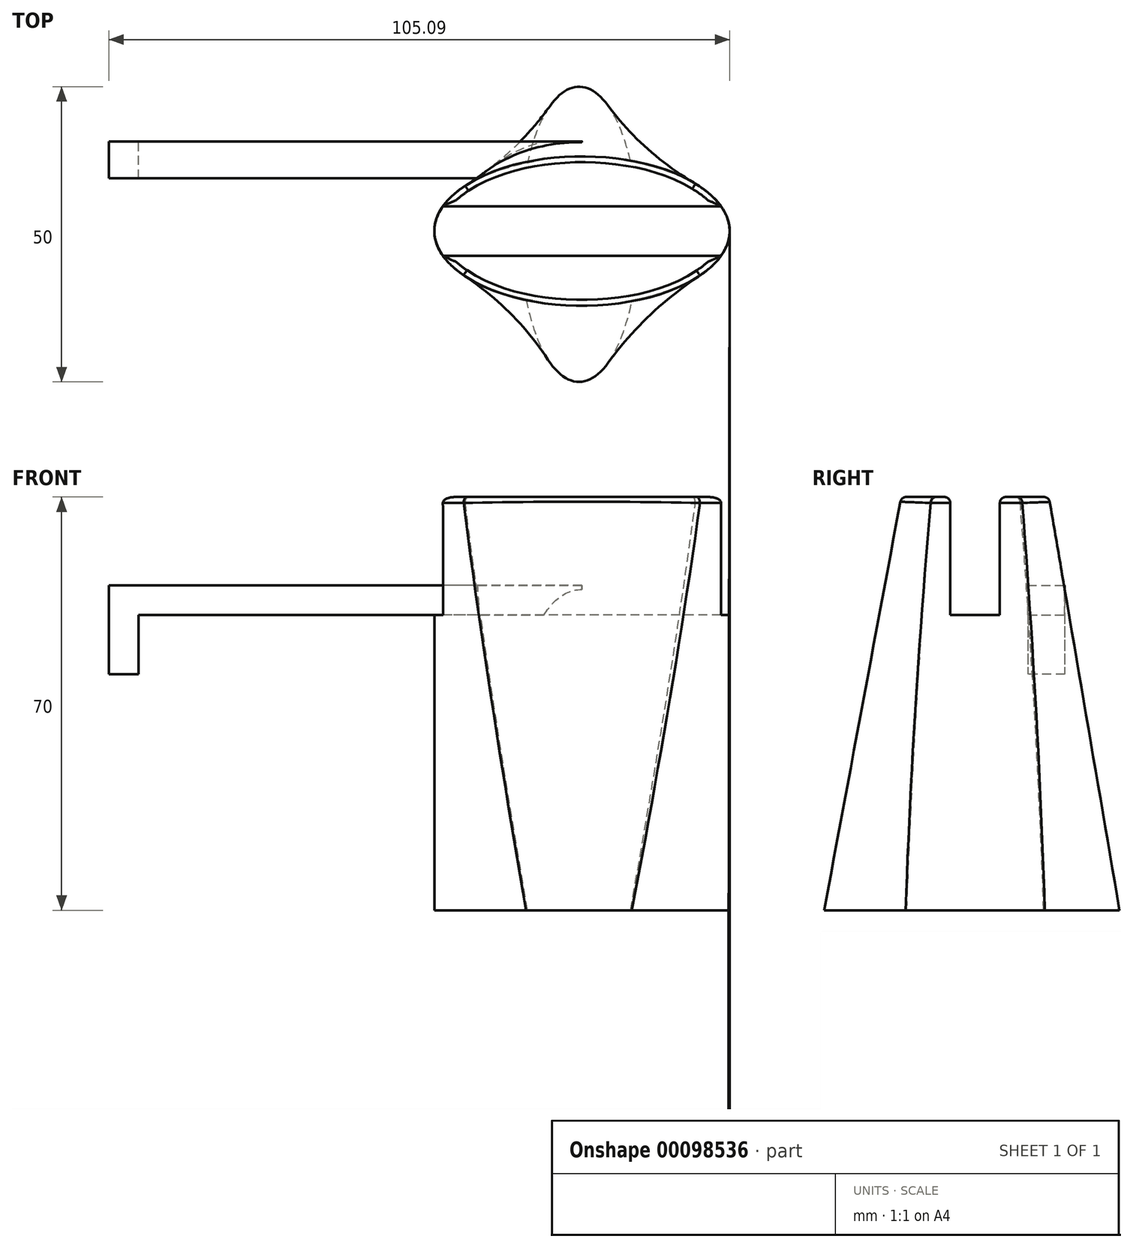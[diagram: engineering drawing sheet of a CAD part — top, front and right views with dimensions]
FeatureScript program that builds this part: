
annotation { "Feature Type Name" : "Feature", "Feature Type Description" : "" }
export const myFeature = defineFeature(function(context is Context, id is Id, definition is map)
    precondition{}
    {
        {
            var Q0;
            Q0=qCreatedBy(makeId("Top.planeOp"),FACE);
            var sketch = newSketch(context, id + "F0", { "sketchPlane" : qUnion([Q0])});
            skEllipse(sketch, "E0", {"center": v(0, 0) * mm, "majorRadius": 25 * mm, "minorRadius": 12.5 * mm, "majorAxis": v(1, 0)});
            skSolve(sketch);
        }
        {
            var Q0;
            Q0=qCreatedBy(makeId("Top.planeOp"),FACE);
            var sketch = newSketch(context, id + "F1", { "sketchPlane" : qUnion([Q0])});
            skEllipse(sketch, "E1", {"center": v(-0.48, -0.55) * mm, "majorRadius": 25 * mm, "minorRadius": 10 * mm, "majorAxis": v(0, 1)});
            skSolve(sketch);
        }
        {
            var Q0;
            Q0=qCreatedBy(makeId("Top.planeOp"),FACE);
            cPlane(context, id + "F2", {"entities" : qUnion([Q0]), "cplaneType" : CPlaneType.OFFSET, "offset" : 70 * mm, "width" : 150 * mm, "height" : 150 * mm});
        }
        {
            var Q0;
            Q0=qCreatedBy(id+"F2.planeOp",FACE);
            var sketch = newSketch(context, id + "F3", { "sketchPlane" : qUnion([Q0])});
            skEllipse(sketch, "E2", {"center": v(0, 0) * mm, "majorRadius": 25 * mm, "minorRadius": 12.5 * mm, "majorAxis": v(1, 0)});
            skSolve(sketch);
        }
        {
            var Q0;
            Q0=makeQuery(id+"F1.imprint","IMPRINT",FACE,{"disambiguationData":[TD([[makeQuery(id+"F1.imprint","IMPRINT",EDGE,{"derivedFrom":sQuery(id+"F1.wireOp",EDGE,"E1")}),1.0]])]});
            var Q1;
            Q1=makeQuery(id+"F3.imprint","IMPRINT",FACE,{"disambiguationData":[TD([[makeQuery(id+"F3.imprint","IMPRINT",EDGE,{"derivedFrom":sQuery(id+"F3.wireOp",EDGE,"E2")}),1.0]])]});
            loft(context, id + "F4", {"sheetProfilesArray" : [{ "sheetProfileEntities" : qUnion([Q0]) }, { "sheetProfileEntities" : qUnion([Q1]) }]});
        }
        {
            var Q1;
            Q1=makeQuery(id+"F0.imprint","IMPRINT",FACE,{"disambiguationData":[TD([[makeQuery(id+"F0.imprint","IMPRINT",EDGE,{"derivedFrom":sQuery(id+"F0.wireOp",EDGE,"E0")}),1.0]])]});
            var Q2;
            Q2=makeQuery(id+"F4.opLoft","CAP_FACE",FACE,{"disambiguationData":[OSD([makeQuery(id+"F3.imprint","IMPRINT",FACE,{"disambiguationData":[TD([[makeQuery(id+"F3.imprint","IMPRINT",EDGE,{"derivedFrom":sQuery(id+"F3.wireOp",EDGE,"E2")}),1.0]])]})])],"isStart":true});
            loft(context, id + "F5", {"operationType" : NewBodyOperationType.ADD, "sheetProfilesArray" : [{ "sheetProfileEntities" : qUnion([Q1]) }, { "sheetProfileEntities" : qUnion([Q2]) }]});
        }
        {
            var Q0;
            Q0=makeQuery(id+"F4.opLoft","CAP_FACE",FACE,{"disambiguationData":[OSD([makeQuery(id+"F3.imprint","IMPRINT",FACE,{"disambiguationData":[TD([[makeQuery(id+"F3.imprint","IMPRINT",EDGE,{"derivedFrom":sQuery(id+"F3.wireOp",EDGE,"E2")}),1.0]])]})])],"isStart":true});
            var sketch = newSketch(context, id + "F6", { "sketchPlane" : qUnion([Q0])});
            skLineSegment(sketch, "E3.bottom", {"start": v(25.13, 4.2) * mm, "end": v(-25.13, 4.2) * mm});
            skLineSegment(sketch, "E3.top", {"start": v(25.13, -4.2) * mm, "end": v(-25.13, -4.2) * mm});
            skLineSegment(sketch, "E3.left", {"start": v(25.13, 4.2) * mm, "end": v(25.13, -4.2) * mm});
            skLineSegment(sketch, "E3.right", {"start": v(-25.13, 4.2) * mm, "end": v(-25.13, -4.2) * mm});
            skPoint(sketch, "E3.middle", {"position": v(0, 0) * mm});
            skSolve(sketch);
        }
        {
            var Q0;
            {var subQ1=sQuery(id+"F3.wireOp",EDGE,"E2");var subQ2=sQuery(id+"F1.wireOp",EDGE,"E1");var subQ3=makeQuery(id+"F5.opLoft","MID_CAP_EDGE",EDGE,{"disambiguationData":[OSD([sQuery(id+"F0.wireOp",EDGE,"E0"),subQ2,subQ1])],"capPos":1.0});var subQ4=makeQuery(id+"F4.opLoft","MID_CAP_EDGE",EDGE,{"disambiguationData":[OSD([subQ2,subQ1])],"capPos":1.0});var subQ8=makeQuery(id+"F5.boolean.opBoolean","MERGE",EDGE,{"disambiguationData":[OD(1.0)],"derivedFrom":[subQ4,subQ3]});var subQ10=sQuery(id+"F6.wireOp",EDGE,"E3.bottom");var subQ12=makeQuery(id+"F6.imprint","INTERSECT",VERTEX,{"derivedFrom":[subQ8,subQ10]});Q0=makeQuery(id+"F6.imprint","IMPRINT",FACE,{"disambiguationData":[TD([[makeQuery(id+"F6.imprint","IMPRINT",EDGE,{"disambiguationData":[TD([[subQ12,-1.0]])],"derivedFrom":subQ10}),1.0]])]});}
            extrude(context, id + "F7", {"entities" : qUnion([Q0]), "operationType" : NewBodyOperationType.REMOVE, "oppositeDirection" : true, "depth" : 20 * mm});
        }
        {
            var Q0;
            {var subQ0=sQuery(id+"F3.wireOp",EDGE,"E2");Q0=makeQuery(id+"F7.boolean.opBoolean","SPLIT",FACE,{"disambiguationData":[TD([makeQuery(id+"F7.opExtrude","SWEPT_FACE",FACE,{"disambiguationData":[OSD([sQuery(id+"F6.wireOp",EDGE,"E3.bottom")])]})])],"derivedFrom":makeQuery(id+"F4.opLoft","CAP_FACE",FACE,{"disambiguationData":[OSD([makeQuery(id+"F3.imprint","IMPRINT",FACE,{"disambiguationData":[TD([[makeQuery(id+"F3.imprint","IMPRINT",EDGE,{"derivedFrom":subQ0}),1.0]])]})])],"isStart":true})});}
            var Q1;
            {var subQ0=sQuery(id+"F3.wireOp",EDGE,"E2");Q1=makeQuery(id+"F7.boolean.opBoolean","SPLIT",FACE,{"disambiguationData":[TD([makeQuery(id+"F7.opExtrude","SWEPT_FACE",FACE,{"disambiguationData":[OSD([sQuery(id+"F6.wireOp",EDGE,"E3.top")])]})])],"derivedFrom":makeQuery(id+"F4.opLoft","CAP_FACE",FACE,{"disambiguationData":[OSD([makeQuery(id+"F3.imprint","IMPRINT",FACE,{"disambiguationData":[TD([[makeQuery(id+"F3.imprint","IMPRINT",EDGE,{"derivedFrom":subQ0}),1.0]])]})])],"isStart":true})});}
            fillet(context, id + "F8", {"entities" : qUnion([Q0, Q1]), "radius" : 1 * mm, "tangentPropagation" : true, "allowEdgeOverflow" : false});
        }
        {
            var Q0;
            Q0=makeQuery(id+"F7.boolean.opBoolean","COPY",FACE,{"derivedFrom":makeQuery(id+"F7.opExtrude","CAP_FACE",FACE,{"disambiguationData":[OSD([sQuery(id+"F0.wireOp",EDGE,"E0"),sQuery(id+"F1.wireOp",EDGE,"E1"),sQuery(id+"F3.wireOp",EDGE,"E2"),sQuery(id+"F6.wireOp",EDGE,"E3.bottom"),sQuery(id+"F6.wireOp",EDGE,"E3.top")])],"isStart":false})});
            cPlane(context, id + "F9", {"entities" : qUnion([Q0]), "cplaneType" : CPlaneType.OFFSET, "offset" : 0 * mm, "width" : 150 * mm, "height" : 150 * mm});
        }
        {
            var Q0;
            Q0=qCreatedBy(id+"F9.planeOp",FACE);
            var sketch = newSketch(context, id + "F10", { "sketchPlane" : qUnion([Q0])});
            skLineSegment(sketch, "E4.bottom", {"start": v(0, 8.92) * mm, "end": v(-75.1, 8.92) * mm});
            skLineSegment(sketch, "E4.top", {"start": v(0, 15.18) * mm, "end": v(-75.1, 15.18) * mm});
            skLineSegment(sketch, "E4.left", {"start": v(0, 8.92) * mm, "end": v(0, 15.18) * mm});
            skLineSegment(sketch, "E4.right", {"start": v(-75.1, 8.92) * mm, "end": v(-75.1, 15.18) * mm});
            skSolve(sketch);
        }
        {
            var Q0;
            Q0=makeQuery(id+"F10.imprint","IMPRINT",FACE,{"disambiguationData":[TD([[makeQuery(id+"F10.imprint","IMPRINT",EDGE,{"derivedFrom":sQuery(id+"F10.wireOp",EDGE,"E4.top")}),1.0]])]});
            extrude(context, id + "F11", {"entities" : qUnion([Q0]), "operationType" : NewBodyOperationType.ADD, "depth" : 5 * mm});
        }
        {
            var Q0;
            Q0=makeQuery(id+"F11.opExtrude","SWEPT_FACE",FACE,{"disambiguationData":[OSD([sQuery(id+"F10.wireOp",EDGE,"E4.right")])]});
            var sketch = newSketch(context, id + "F12", { "sketchPlane" : qUnion([Q0])});
            skLineSegment(sketch, "E5.bottom", {"start": v(-15.18, 55) * mm, "end": v(-8.92, 55) * mm});
            skLineSegment(sketch, "E5.top", {"start": v(-15.18, 40) * mm, "end": v(-8.92, 40) * mm});
            skLineSegment(sketch, "E5.left", {"start": v(-15.18, 55) * mm, "end": v(-15.18, 40) * mm});
            skLineSegment(sketch, "E5.right", {"start": v(-8.92, 55) * mm, "end": v(-8.92, 40) * mm});
            skSolve(sketch);
        }
        {
            var Q0;
            Q0 = qSketchRegion(id + "F12", true);
            extrude(context, id + "F13", {"entities" : qUnion([Q0]), "operationType" : NewBodyOperationType.ADD, "depth" : 5 * mm});
        }
    });
